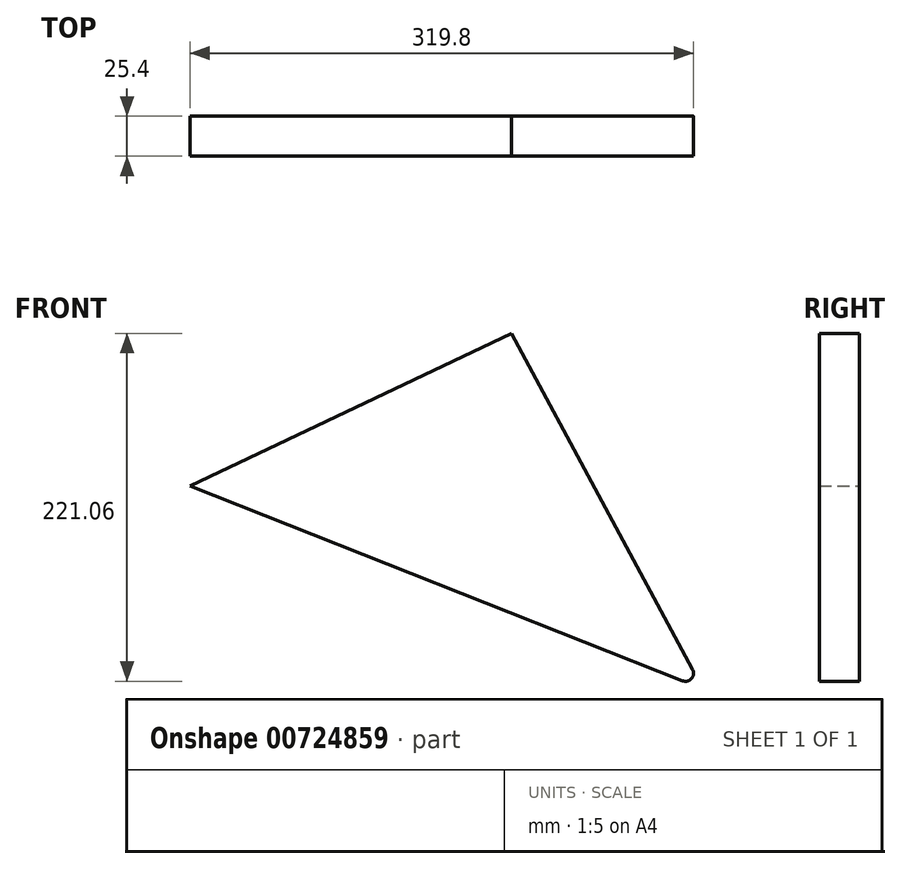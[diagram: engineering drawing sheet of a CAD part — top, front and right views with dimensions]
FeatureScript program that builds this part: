
annotation { "Feature Type Name" : "Feature", "Feature Type Description" : "" }
export const myFeature = defineFeature(function(context is Context, id is Id, definition is map)
    precondition{}
    {
        {
            var Q0;
            Q0=qCreatedBy(makeId("Front.planeOp"),FACE);
            var sketch = newSketch(context, id + "F0", { "sketchPlane" : qUnion([Q0])});
            skLineSegment(sketch, "E0", {"start": v(-204.1, -97.1) * mm, "end": v(0, 0) * mm});
            skLineSegment(sketch, "E1", {"start": v(0, 0) * mm, "end": v(121.7, -225.81) * mm});
            skLineSegment(sketch, "E2", {"start": v(121.7, -225.81) * mm, "end": v(-204.1, -97.1) * mm});
            skSolve(sketch);
        }
        {
            var Q0;
            Q0=makeQuery(id+"F0.imprint","IMPRINT",FACE,{"disambiguationData":[TD([[makeQuery(id+"F0.imprint","IMPRINT",EDGE,{"derivedFrom":sQuery(id+"F0.wireOp",EDGE,"E0")}),-1.0]])]});
            extrude(context, id + "F1", {"entities" : qUnion([Q0]), "depth" : 25.4 * mm, "offsetDistance" : 25.4 * mm});
        }
        {
            var Q0;
            Q0=makeQuery(id+"F1.opExtrude","SWEPT_EDGE",EDGE,{"disambiguationData":[OSD([sQuery(id+"F0.wireOp",EDGE,"E1"),sQuery(id+"F0.wireOp",EDGE,"E2")])]});
            fillet(context, id + "F2", {"entities" : qUnion([Q0]), "radius" : 5.08 * mm, "tangentPropagation" : true, "allowEdgeOverflow" : false});
        }
    });
